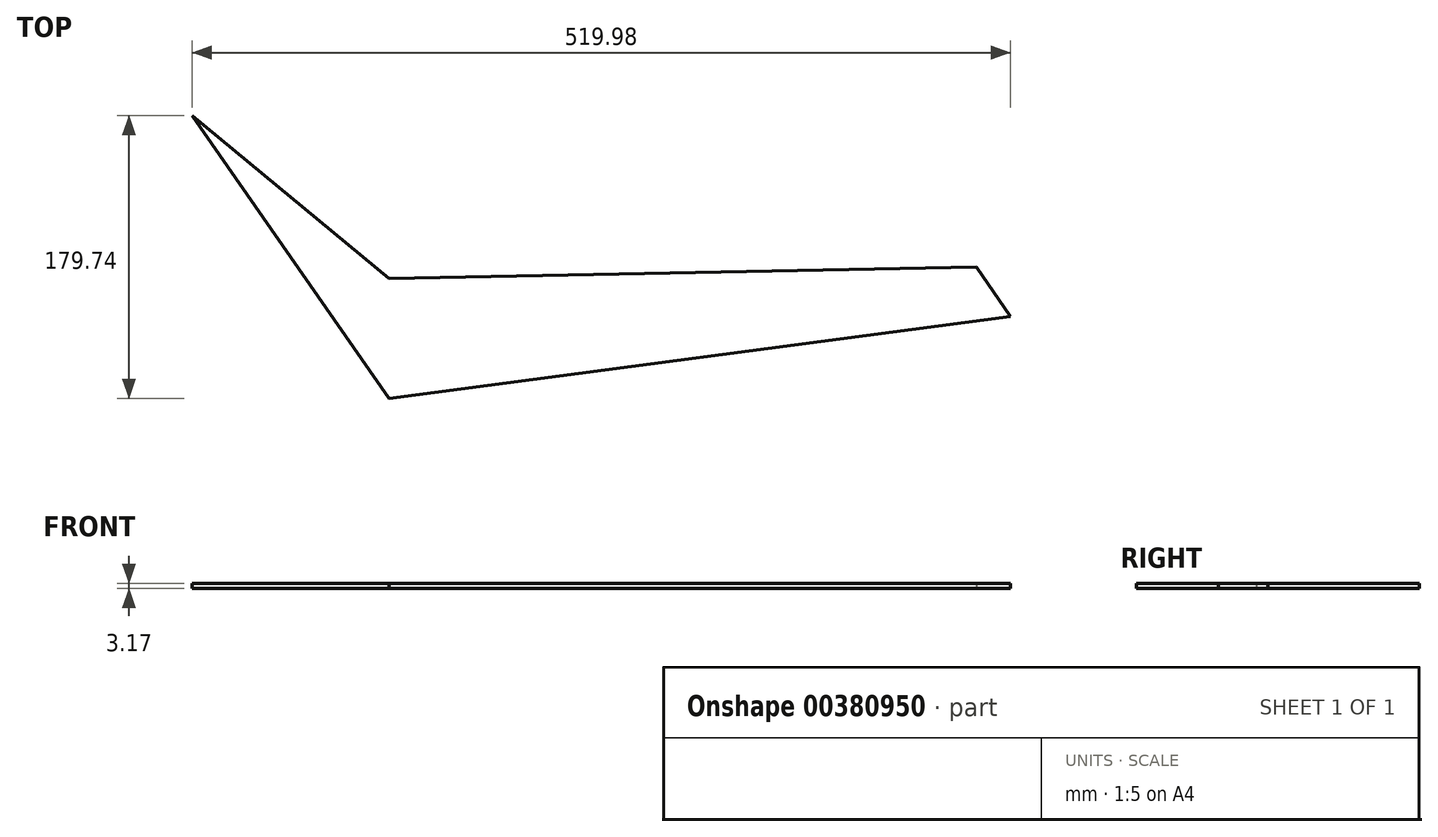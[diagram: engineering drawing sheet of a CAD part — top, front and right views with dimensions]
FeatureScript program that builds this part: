
annotation { "Feature Type Name" : "Feature", "Feature Type Description" : "" }
export const myFeature = defineFeature(function(context is Context, id is Id, definition is map)
    precondition{}
    {
        {
            var Q0;
            Q0=qCreatedBy(makeId("Top.planeOp"),FACE);
            var sketch = newSketch(context, id + "F0", { "sketchPlane" : qUnion([Q0])});
            skLineSegment(sketch, "E0.bottom", {"start": v(-186.48, 34.52) * mm, "end": v(186.48, 41.68) * mm});
            skPoint(sketch, "E0.middle", {"position": v(0, 0) * mm});
            skLineSegment(sketch, "E1", {"start": v(-186.48, -41.68) * mm, "end": v(-311.72, 138.06) * mm});
            skLineSegment(sketch, "E2", {"start": v(-311.72, 138.06) * mm, "end": v(-186.48, 34.52) * mm});
            skLineSegment(sketch, "E3", {"start": v(186.48, 41.68) * mm, "end": v(244.56, -41.68) * mm});
            skLineSegment(sketch, "E4", {"start": v(186.48, 41.68) * mm, "end": v(208.26, 10.42) * mm});
            skLineSegment(sketch, "E5", {"start": v(-186.48, -41.68) * mm, "end": v(208.26, 10.42) * mm});
            skSolve(sketch);
        }
        {
            var Q0;
            Q0=qSketchRegion(id+"F0",true);
            extrude(context, id + "F1", {"entities" : qUnion([Q0]), "depth" : 3.17 * mm});
        }
    });
